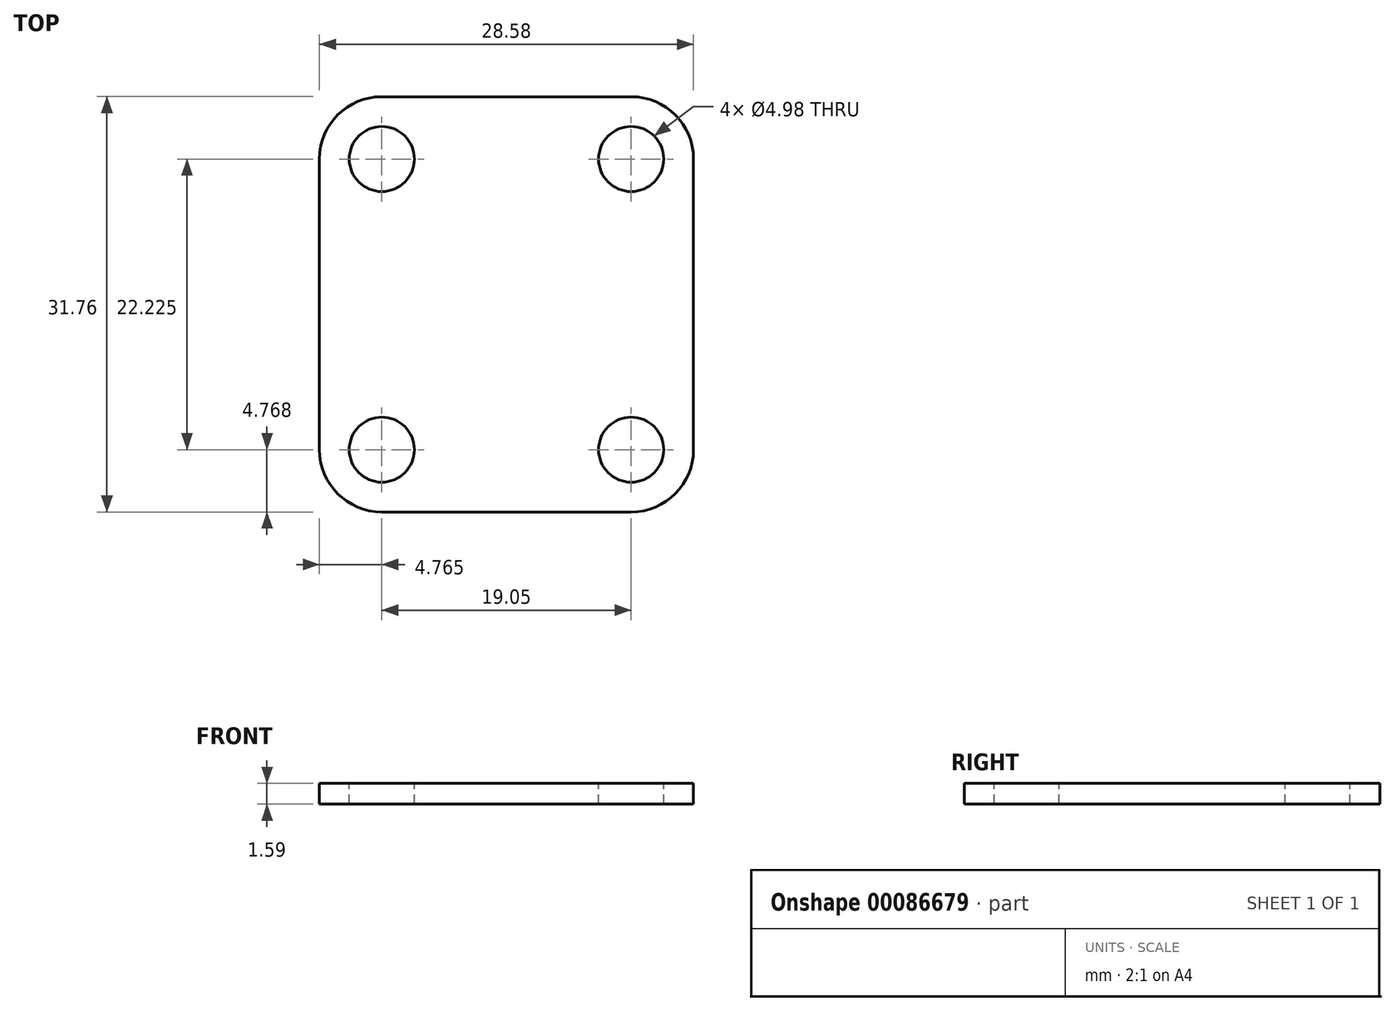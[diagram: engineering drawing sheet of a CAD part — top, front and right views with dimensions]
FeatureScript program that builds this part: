
annotation { "Feature Type Name" : "Feature", "Feature Type Description" : "" }
export const myFeature = defineFeature(function(context is Context, id is Id, definition is map)
    precondition{}
    {
        {
            var Q0;
            Q0=qCreatedBy(makeId("Top.planeOp"),FACE);
            var sketch = newSketch(context, id + "F0", { "sketchPlane" : qUnion([Q0])});
            skLineSegment(sketch, "E0.bottom", {"start": v(14.29, -15.88) * mm, "end": v(-14.29, -15.88) * mm});
            skLineSegment(sketch, "E0.top", {"start": v(14.29, 15.88) * mm, "end": v(-14.29, 15.87) * mm});
            skLineSegment(sketch, "E0.left", {"start": v(14.29, -15.88) * mm, "end": v(14.29, 15.88) * mm});
            skLineSegment(sketch, "E0.right", {"start": v(-14.29, -15.88) * mm, "end": v(-14.29, 15.87) * mm});
            skPoint(sketch, "E0.middle", {"position": v(0, 0) * mm});
            skSolve(sketch);
        }
        {
            var Q0;
            Q0=makeQuery(id+"F0.imprint","IMPRINT",FACE,{"disambiguationData":[TD([[makeQuery(id+"F0.imprint","IMPRINT",EDGE,{"derivedFrom":sQuery(id+"F0.wireOp",EDGE,"E0.bottom")}),-1.0]])]});
            extrude(context, id + "F1", {"entities" : qUnion([Q0]), "depth" : 1.59 * mm});
        }
        {
            var Q0;
            Q0=makeQuery(id+"F1.opExtrude","CAP_FACE",FACE,{"disambiguationData":[OSD([sQuery(id+"F0.wireOp",EDGE,"E0.bottom"),sQuery(id+"F0.wireOp",EDGE,"E0.top"),sQuery(id+"F0.wireOp",EDGE,"E0.left"),sQuery(id+"F0.wireOp",EDGE,"E0.right")])],"isStart":false});
            var sketch = newSketch(context, id + "F2", { "sketchPlane" : qUnion([Q0])});
            skLineSegment(sketch, "E1.bottom", {"start": v(4.76, -6.35) * mm, "end": v(-4.76, -6.35) * mm, "construction": true});
            skLineSegment(sketch, "E1.top", {"start": v(4.76, 6.35) * mm, "end": v(-4.76, 6.35) * mm, "construction": true});
            skLineSegment(sketch, "E1.left", {"start": v(4.76, -6.35) * mm, "end": v(4.76, 6.35) * mm, "construction": true});
            skLineSegment(sketch, "E1.right", {"start": v(-4.76, -6.35) * mm, "end": v(-4.76, 6.35) * mm, "construction": true});
            skPoint(sketch, "E1.middle", {"position": v(0, 0) * mm});
            skLineSegment(sketch, "E2", {"start": v(-4.76, 6.35) * mm, "end": v(-14.29, 15.87) * mm, "construction": true});
            skLineSegment(sketch, "E3", {"start": v(-14.29, 15.87) * mm, "end": v(-9.53, 11.11) * mm, "construction": true});
            skLineSegment(sketch, "E4", {"start": v(4.76, 6.35) * mm, "end": v(14.29, 15.88) * mm, "construction": true});
            skLineSegment(sketch, "E5", {"start": v(14.29, 15.88) * mm, "end": v(9.53, 11.11) * mm, "construction": true});
            skLineSegment(sketch, "E6", {"start": v(-4.76, -6.35) * mm, "end": v(-14.29, -15.88) * mm, "construction": true});
            skLineSegment(sketch, "E7", {"start": v(-14.29, -15.88) * mm, "end": v(-9.53, -11.11) * mm, "construction": true});
            skLineSegment(sketch, "E8", {"start": v(4.76, -6.35) * mm, "end": v(14.29, -15.88) * mm, "construction": true});
            skLineSegment(sketch, "E9", {"start": v(14.29, -15.88) * mm, "end": v(9.52, -11.11) * mm, "construction": true});
            skSolve(sketch);
        }
        {
            var Q0;
            Q0=sQuery(id+"F2.wireOp",VERTEX,"E3.end");
            var Q1;
            Q1=sQuery(id+"F2.wireOp",VERTEX,"E5.end");
            var Q2;
            Q2=sQuery(id+"F2.wireOp",VERTEX,"E9.end");
            var Q3;
            Q3=sQuery(id+"F2.wireOp",VERTEX,"E7.end");
            var Q4;
            Q4=makeQuery(id+"F1.opExtrude","SWEPT_BODY",BODY,{"disambiguationData":[OSD([sQuery(id+"F0.wireOp",EDGE,"E0.bottom"),sQuery(id+"F0.wireOp",EDGE,"E0.top"),sQuery(id+"F0.wireOp",EDGE,"E0.left"),sQuery(id+"F0.wireOp",EDGE,"E0.right")])]});
            hole(context, id + "F3", {"style" : HoleStyle.SIMPLE, "endStyle" : HoleEndStyle.THROUGH, "holeDiameter" : 4.98 * mm, "locations" : qUnion([Q0, Q1, Q2, Q3]), "scope" : qUnion([Q4]), "isTappedThrough" : true});
        }
        {
            var Q0;
            Q0=makeQuery(id+"F1.opExtrude","SWEPT_EDGE",EDGE,{"disambiguationData":[OSD([sQuery(id+"F0.wireOp",EDGE,"E0.bottom"),sQuery(id+"F0.wireOp",EDGE,"E0.left")])]});
            var Q1;
            Q1=makeQuery(id+"F1.opExtrude","SWEPT_EDGE",EDGE,{"disambiguationData":[OSD([sQuery(id+"F0.wireOp",EDGE,"E0.bottom"),sQuery(id+"F0.wireOp",EDGE,"E0.right")])]});
            var Q2;
            Q2=makeQuery(id+"F1.opExtrude","SWEPT_EDGE",EDGE,{"disambiguationData":[OSD([sQuery(id+"F0.wireOp",EDGE,"E0.top"),sQuery(id+"F0.wireOp",EDGE,"E0.left")])]});
            var Q3;
            Q3=makeQuery(id+"F1.opExtrude","SWEPT_EDGE",EDGE,{"disambiguationData":[OSD([sQuery(id+"F0.wireOp",EDGE,"E0.top"),sQuery(id+"F0.wireOp",EDGE,"E0.right")])]});
            fillet(context, id + "F4", {"entities" : qUnion([Q0, Q1, Q2, Q3]), "radius" : 4.76 * mm, "tangentPropagation" : true, "allowEdgeOverflow" : false});
        }
    });
